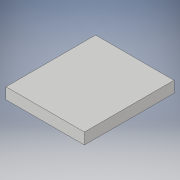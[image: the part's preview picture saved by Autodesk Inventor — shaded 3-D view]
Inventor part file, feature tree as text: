
AUTODESK INVENTOR PART (.ipt)
format: ipt  version: 2019 (Build 230136000, 136)  size: 241,152 bytes
history: native  units: in
note: dims shown in document units (in); Inventor stores cm internally (conversion verified against a paired STEP export)
features: extrude x5, sketch x5
ambient origin geometry x8: Origin, YZ Plane, XZ Plane, XY Plane, X Axis, Y Axis, Z Axis, Center Point
bodies: Solid1 (feature_tree)
feature tree (10):
  extrude  "Extrusion1"  Depth=6.2992in
  extrude  "Extrusion2"  Depth=3.1496in
  sketch  "Sketch3"  dims[d6=0.7874in d7=0.0in d8=3.937in]
  extrude  "Extrusion5"  Depth=0.7874in
  extrude  "Extrusion4"  Depth=0.3937in TaperAngle=0.0deg
  extrude  "Extrusion6"  Depth=0.7874in
  sketch  "Sketch1"  dims[d0=5.5118in d1=6.2992in]
  sketch  "Sketch2"  dims[d4=2.7559in d5=3.1496in]
  sketch  "Sketch4"  dims[d9=4.7244in d10=0.3937in d11=0.0in]
  sketch  "Sketch5"  dims[d12=0.7874in d13=0.7874in d14=0.7874in d15=0.7874in d16=0.7874in d17=0.7874in d18=0.7874in d19=0.7874in d20=0.7874in d21=0.7874in d22=0.7874in d23=0.7874in d25=0.7874in d26=0.7874in d27=0.7874in d28=0.7874in d29=0.7874in d30=0.7874in d31=0.7874in d32=0.7874in d33=0.7874in d34=0.7874in d35=0.7874in d36=0.7874in d37=0.7874in d38=0.7874in d39=0.7874in d40=0.7874in d41=0.7874in d42=0.7874in d43=0.7874in d44=0.7874in d45=0.7874in d46=0.7874in d47=0.7874in d48=0.7874in d49=0.7874in d50=0.7874in d53=0.1969in d54=0.1969in d55=0.1969in d56=0.1969in d57=4.7244in d58=3.5433in d63=0.4823in d73=0.1969in d75=0.3937in d76=0.0in d77=0.7874in d78=0.7874in d79=0.7874in d80=0.7874in d81=0.7874in d82=0.7874in d83=0.7874in d84=0.7874in d85=0.7874in d86=0.3937in d87=0.0in d88=0.1969in d90=0.1969in d91=0.3937in d92=0.0in]
